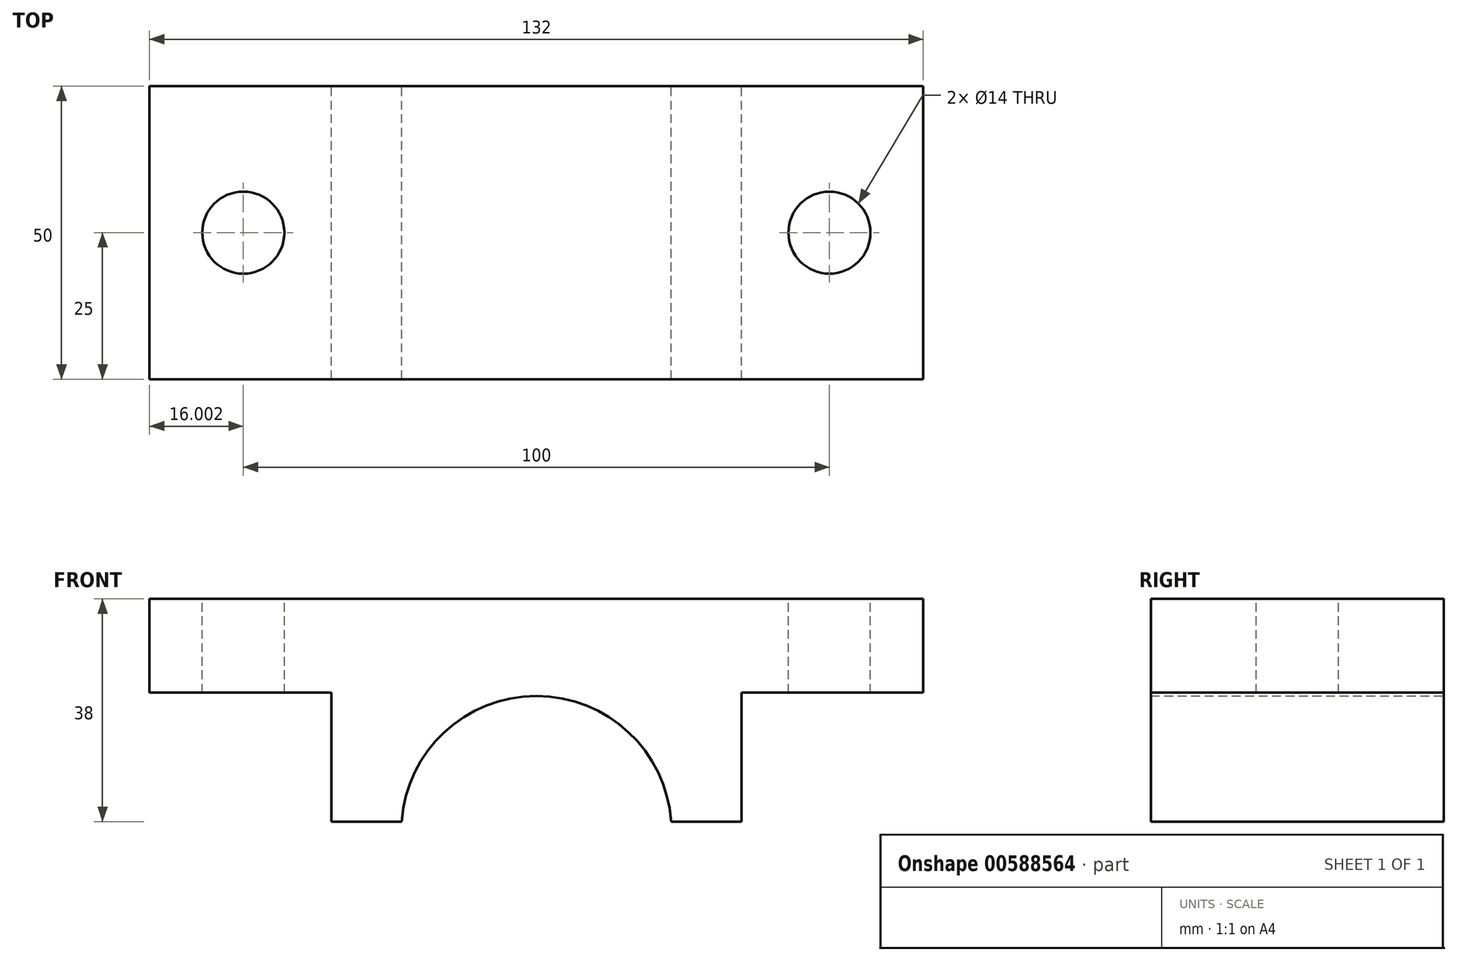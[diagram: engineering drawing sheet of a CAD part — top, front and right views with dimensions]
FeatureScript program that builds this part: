
annotation { "Feature Type Name" : "Feature", "Feature Type Description" : "" }
export const myFeature = defineFeature(function(context is Context, id is Id, definition is map)
    precondition{}
    {
        {
            var Q0;
            Q0=qCreatedBy(makeId("Front.planeOp"),FACE);
            var sketch = newSketch(context, id + "F0", { "sketchPlane" : qUnion([Q0])});
            skLineSegment(sketch, "E0", {"start": v(-61.68, 0) * mm, "end": v(70.32, 0) * mm});
            skLineSegment(sketch, "E1", {"start": v(70.32, 0) * mm, "end": v(70.32, -16) * mm});
            skLineSegment(sketch, "E2", {"start": v(70.32, -16) * mm, "end": v(39.32, -16) * mm});
            skLineSegment(sketch, "E3", {"start": v(39.32, -16) * mm, "end": v(39.32, -38) * mm});
            skLineSegment(sketch, "E4", {"start": v(39.32, -38) * mm, "end": v(27.32, -38) * mm});
            skLineSegment(sketch, "E5", {"start": v(-30.68, -38) * mm, "end": v(-30.68, -16) * mm});
            skLineSegment(sketch, "E6", {"start": v(-61.68, 0) * mm, "end": v(-61.68, -16) * mm});
            skLineSegment(sketch, "E7", {"start": v(-61.68, -16) * mm, "end": v(-30.68, -16) * mm});
            skArc(sketch, "E8", {"start": v(27.32, -38) * mm, "mid": v(4.32, -16.57) * mm, "end": v(-18.68, -38) * mm});
            skPoint(sketch, "E9.end.orphan", {"position": v(-18.68, -33.68) * mm});
            skPoint(sketch, "E10.end.orphan", {"position": v(27.32, -33.68) * mm});
            skPoint(sketch, "E10.start.orphan", {"position": v(39.32, -33.68) * mm});
            skLineSegment(sketch, "E11.trimOffspring", {"start": v(-18.68, -38) * mm, "end": v(-30.68, -38) * mm});
            skSolve(sketch);
        }
        {
            var Q0;
            Q0=makeQuery(id+"F0.imprint","IMPRINT",FACE,{"disambiguationData":[TD([[makeQuery(id+"F0.imprint","IMPRINT",EDGE,{"derivedFrom":sQuery(id+"F0.wireOp",EDGE,"E0")}),-1.0]])]});
            extrude(context, id + "F1", {"entities" : qUnion([Q0]), "depth" : 50 * mm, "offsetDistance" : 25 * mm});
        }
        {
            var Q0;
            Q0=makeQuery(id+"F1.opExtrude","SWEPT_FACE",FACE,{"disambiguationData":[OSD([sQuery(id+"F0.wireOp",EDGE,"E0")])]});
            var sketch = newSketch(context, id + "F2", { "sketchPlane" : qUnion([Q0])});
            skPoint(sketch, "E12.endSnap0", {"position": v(70.32, -25) * mm});
            skCircle(sketch, "E13", {"center": v(-45.68, -25) * mm, "radius": 7 * mm});
            skCircle(sketch, "E14", {"center": v(54.32, -25) * mm, "radius": 7 * mm});
            skPoint(sketch, "E15.center.orphan", {"position": v(76.49, -25) * mm});
            skPoint(sketch, "E16.orphan", {"position": v(-61.68, -25) * mm});
            skSolve(sketch);
        }
        {
            var Q0;
            Q0=makeQuery(id+"F2.imprint","IMPRINT",FACE,{"disambiguationData":[TD([[makeQuery(id+"F2.imprint","IMPRINT",EDGE,{"derivedFrom":sQuery(id+"F2.wireOp",EDGE,"E14")}),1.0]])]});
            var Q1;
            Q1=makeQuery(id+"F2.imprint","IMPRINT",FACE,{"disambiguationData":[TD([[makeQuery(id+"F2.imprint","IMPRINT",EDGE,{"derivedFrom":sQuery(id+"F2.wireOp",EDGE,"E13")}),1.0]])]});
            extrude(context, id + "F3", {"entities" : qUnion([Q0, Q1]), "operationType" : NewBodyOperationType.REMOVE, "oppositeDirection" : true, "depth" : 25 * mm, "offsetDistance" : 25 * mm});
        }
    });
